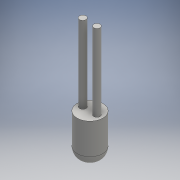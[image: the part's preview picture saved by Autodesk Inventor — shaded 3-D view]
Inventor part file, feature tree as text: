
AUTODESK INVENTOR PART (.ipt)
format: ipt  version: 2016 (Build 200138000, 138)  size: 107,520 bytes
history: native  units: mm
features: extrude x2, sketch x2, fillet x1
ambient origin geometry x8: Origin, YZ Plane, XZ Plane, XY Plane, X Axis, Y Axis, Z Axis, Center Point
bodies: Solid1 (feature_tree)
feature tree (5):
  extrude  "Extrusion1"  Depth=8.0mm TaperAngle=0.0deg
  extrude  "Extrusion2"  Depth=2.0mm
  fillet  "Fillet1"  [1 undecoded]
  sketch  "Sketch1"  dims[d0=5.0mm d1=8.0mm d2=0.0mm]
  sketch  "Sketch2"  dims[d3=15.0mm d4=0.0mm d5=2.0mm]
note: 1 required parameter value undecoded (feature->parameter linkage not recoverable at this tier; creation-order binding heuristic only, values carry confidence <= 0.55)
